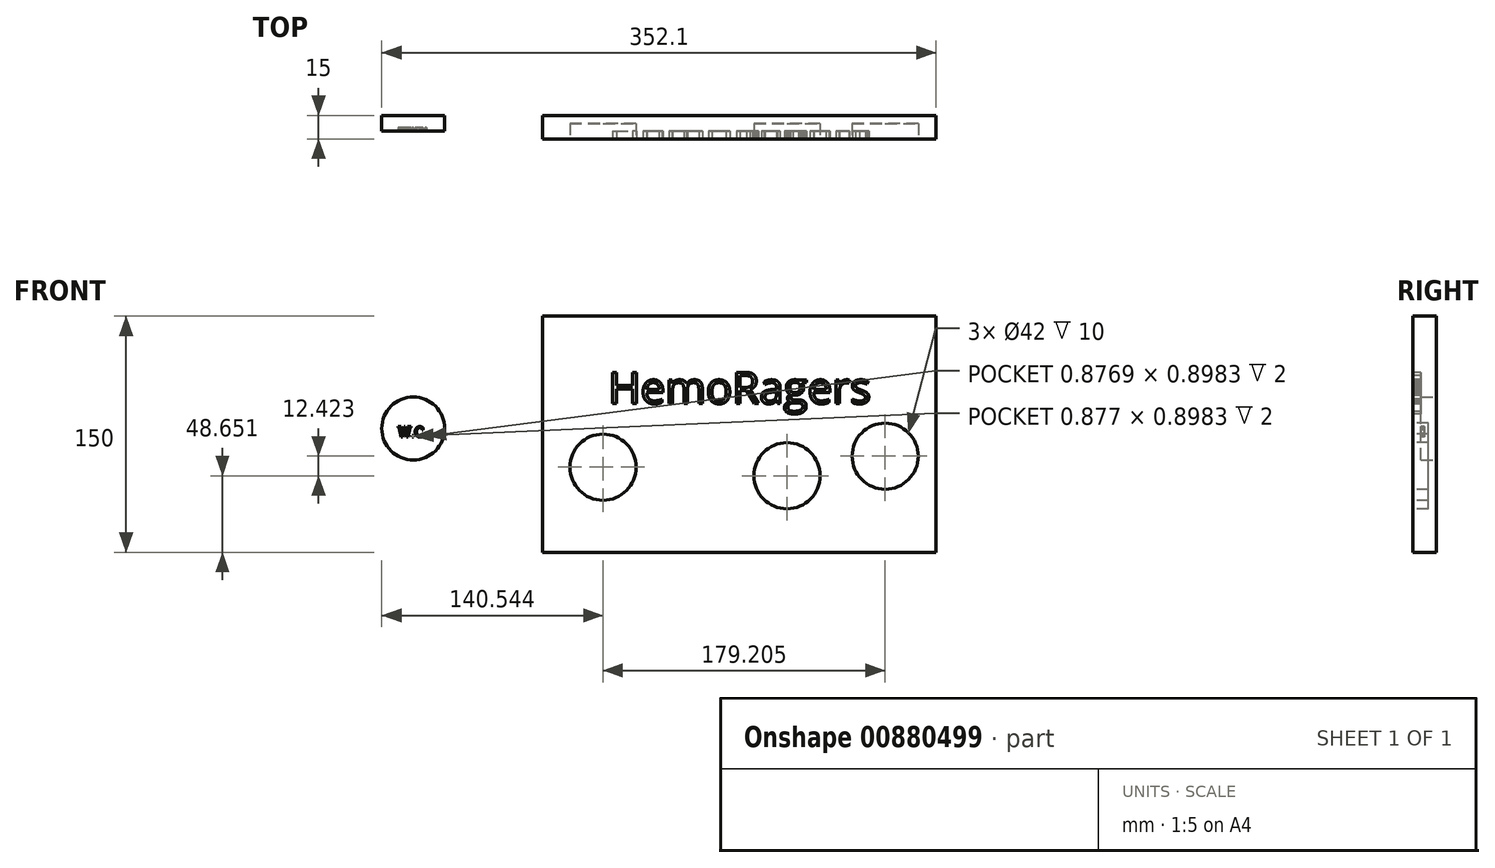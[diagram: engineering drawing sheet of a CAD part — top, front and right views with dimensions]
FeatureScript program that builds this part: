
annotation { "Feature Type Name" : "Feature", "Feature Type Description" : "" }
export const myFeature = defineFeature(function(context is Context, id is Id, definition is map)
    precondition{}
    {
        {
            var Q0;
            Q0=qCreatedBy(makeId("Front.planeOp"),FACE);
            var sketch = newSketch(context, id + "F0", { "sketchPlane" : qUnion([Q0])});
            skLineSegment(sketch, "E0.bottom", {"start": v(-93.81, 70.1) * mm, "end": v(156.19, 70.1) * mm});
            skLineSegment(sketch, "E0.top", {"start": v(-93.81, -79.9) * mm, "end": v(156.19, -79.9) * mm});
            skLineSegment(sketch, "E0.left", {"start": v(-93.81, 70.1) * mm, "end": v(-93.81, -79.9) * mm});
            skLineSegment(sketch, "E0.right", {"start": v(156.19, 70.1) * mm, "end": v(156.19, -79.9) * mm});
            skSolve(sketch);
        }
        {
            var Q0;
            Q0=makeQuery(id+"F0.imprint","IMPRINT",FACE,{"disambiguationData":[TD([[makeQuery(id+"F0.imprint","IMPRINT",EDGE,{"derivedFrom":sQuery(id+"F0.wireOp",EDGE,"E0.bottom")}),-1.0]])]});
            extrude(context, id + "F1", {"entities" : qUnion([Q0]), "depth" : 15 * mm, "offsetDistance" : 25 * mm});
        }
        {
            var Q0;
            Q0=qCreatedBy(makeId("Front.planeOp"),FACE);
            var sketch = newSketch(context, id + "F2", { "sketchPlane" : qUnion([Q0])});
            skCircle(sketch, "E1", {"center": v(-175.9, -1.24) * mm, "radius": 20 * mm});
            skSolve(sketch);
        }
        {
            var Q0;
            Q0 = qSketchRegion(id + "F2", true);
            extrude(context, id + "F3", {"entities" : qUnion([Q0]), "depth" : 9.8 * mm, "offsetDistance" : 25 * mm});
        }
        {
            var Q0;
            Q0=makeQuery(id+"F1.opExtrude","CAP_FACE",FACE,{"disambiguationData":[OSD([sQuery(id+"F0.wireOp",EDGE,"E0.bottom"),sQuery(id+"F0.wireOp",EDGE,"E0.top"),sQuery(id+"F0.wireOp",EDGE,"E0.left"),sQuery(id+"F0.wireOp",EDGE,"E0.right")])],"isStart":false});
            var sketch = newSketch(context, id + "F4", { "sketchPlane" : qUnion([Q0])});
            skCircle(sketch, "E2", {"center": v(-55.37, -25.8) * mm, "radius": 21 * mm});
            skSolve(sketch);
        }
        {
            var Q0;
            Q0 = qSketchRegion(id + "F4", true);
            extrude(context, id + "F5", {"entities" : qUnion([Q0]), "operationType" : NewBodyOperationType.REMOVE, "oppositeDirection" : true, "depth" : 10 * mm, "offsetDistance" : 25 * mm});
        }
        {
            var Q0;
            Q0=makeQuery(id+"F4.imprint","IMPRINT",FACE,{"disambiguationData":[TD([[makeQuery(id+"F4.imprint","IMPRINT",EDGE,{"derivedFrom":sQuery(id+"F4.wireOp",EDGE,"E2")}),-1.0]])]});
            var sketch = newSketch(context, id + "F6", { "sketchPlane" : qUnion([Q0])});
            skText(sketch, "E3", { "text": "HemoRagers\n", "fontName": "OpenSans-Regular.ttf"});
            const initialGuessF6  = {"E3": [-0.05196, 0.01462, 1, 0, 0.02]};
            skSetInitialGuess(sketch, initialGuessF6);
            skSolve(sketch);
        }
        {
            var Q0;
            Q0 = qSketchRegion(id + "F6", true);
            extrude(context, id + "F7", {"entities" : qUnion([Q0]), "operationType" : NewBodyOperationType.REMOVE, "oppositeDirection" : true, "depth" : 5 * mm, "offsetDistance" : 25 * mm});
        }
        {
            var Q0;
            Q0=makeQuery(id+"F3.opExtrude","SWEPT_BODY",BODY,{"disambiguationData":[OSD([sQuery(id+"F2.wireOp",EDGE,"E1")])]});
            transform(context, id + "F8", {"entities" : qUnion([Q0]), "transformType" : TransformType.TRANSLATION_3D, "dx" : 0 * mm, "dy" : 0 * mm, "dz" : 0 * mm, "makeCopy" : true});
        }
        {
            var Q0;
            Q0=makeQuery(id+"F8.opPattern","COPY",BODY,{"derivedFrom":makeQuery(id+"F3.opExtrude","SWEPT_BODY",BODY,{"disambiguationData":[OSD([sQuery(id+"F2.wireOp",EDGE,"E1")])]}),"instanceName":"1"});
            deleteBodies(context, id + "F9", {"entities" : qUnion([Q0])});
        }
        {
            var Q0;
            Q0=makeQuery(id+"F3.opExtrude","SWEPT_BODY",BODY,{"disambiguationData":[OSD([sQuery(id+"F2.wireOp",EDGE,"E1")])]});
            transform(context, id + "F10", {"entities" : qUnion([Q0]), "transformType" : TransformType.TRANSLATION_3D, "dx" : 45 * mm, "dy" : 0 * mm, "dz" : 0 * mm, "makeCopy" : true});
        }
        {
            var Q0;
            Q0=makeQuery(id+"F10.opPattern","COPY",BODY,{"derivedFrom":makeQuery(id+"F3.opExtrude","SWEPT_BODY",BODY,{"disambiguationData":[OSD([sQuery(id+"F2.wireOp",EDGE,"E1")])]}),"instanceName":"1"});
            deleteBodies(context, id + "F11", {"entities" : qUnion([Q0])});
        }
        {
            var Q0;
            Q0=makeQuery(id+"F6.imprint","IMPRINT",FACE,{"disambiguationData":[TD([[makeQuery(id+"F6.imprint","IMPRINT",EDGE,{"derivedFrom":sQuery(id+"F6.wireOp",EDGE,"E3.sketch_text.stroke-0")}),1.0]])]});
            var sketch = newSketch(context, id + "F12", { "sketchPlane" : qUnion([Q0])});
            skCircle(sketch, "E4", {"center": v(61.54, -31.26) * mm, "radius": 21 * mm});
            skSolve(sketch);
        }
        {
            var Q0;
            Q0 = qSketchRegion(id + "F12", true);
            extrude(context, id + "F13", {"entities" : qUnion([Q0]), "operationType" : NewBodyOperationType.REMOVE, "oppositeDirection" : true, "depth" : 10 * mm, "offsetDistance" : 25 * mm});
        }
        {
            var Q0;
            Q0=makeQuery(id+"F4.imprint","IMPRINT",FACE,{"disambiguationData":[TD([[makeQuery(id+"F4.imprint","IMPRINT",EDGE,{"derivedFrom":sQuery(id+"F4.wireOp",EDGE,"E2")}),-1.0]])]});
            var sketch = newSketch(context, id + "F14", { "sketchPlane" : qUnion([Q0])});
            skCircle(sketch, "E5", {"center": v(123.84, -18.84) * mm, "radius": 21 * mm});
            skSolve(sketch);
        }
        {
            var Q0;
            Q0 = qSketchRegion(id + "F14", true);
            extrude(context, id + "F15", {"entities" : qUnion([Q0]), "operationType" : NewBodyOperationType.REMOVE, "oppositeDirection" : true, "depth" : 10 * mm, "offsetDistance" : 25 * mm});
        }
        {
            var Q0;
            Q0=makeQuery(id+"F3.opExtrude","CAP_FACE",FACE,{"disambiguationData":[OSD([sQuery(id+"F2.wireOp",EDGE,"E1")])],"isStart":false});
            var sketch = newSketch(context, id + "F16", { "sketchPlane" : qUnion([Q0])});
            skText(sketch, "E6", { "text": "W.C.\n", "fontName": "RobotoSlab-Regular.ttf"});
            const initialGuessF16  = {"E6": [-0.18564, -0.00656, 1, 0, 0.00656]};
            skSetInitialGuess(sketch, initialGuessF16);
            skSolve(sketch);
        }
        {
            var Q0;
            Q0 = qSketchRegion(id + "F16", true);
            extrude(context, id + "F17", {"entities" : qUnion([Q0]), "operationType" : NewBodyOperationType.REMOVE, "oppositeDirection" : true, "depth" : 2 * mm, "offsetDistance" : 25 * mm});
        }
    });
